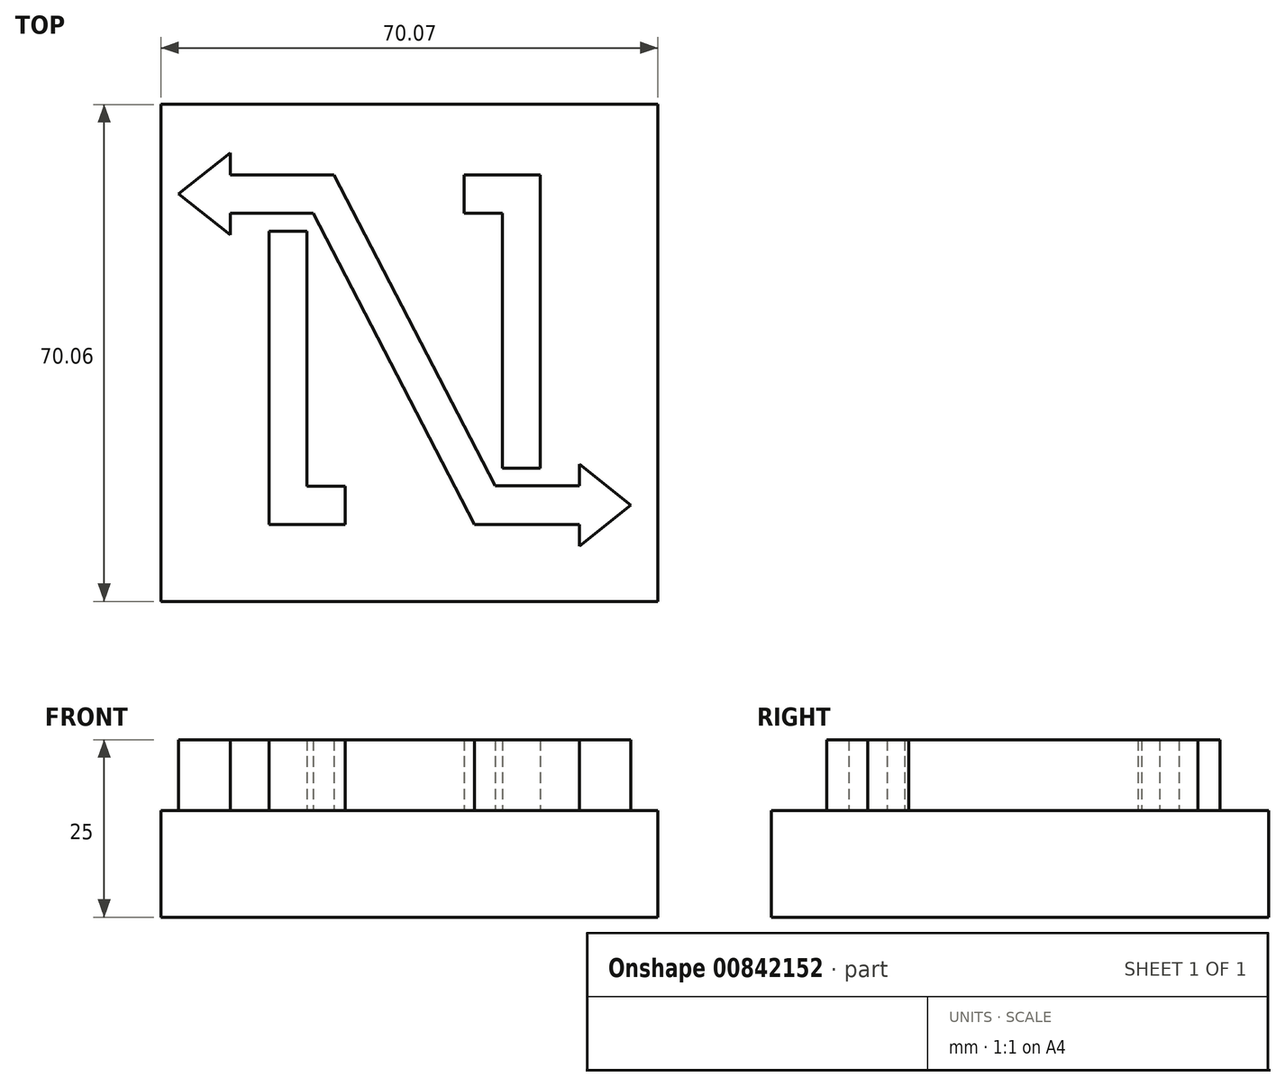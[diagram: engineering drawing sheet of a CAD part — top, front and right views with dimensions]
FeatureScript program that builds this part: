
annotation { "Feature Type Name" : "Feature", "Feature Type Description" : "" }
export const myFeature = defineFeature(function(context is Context, id is Id, definition is map)
    precondition{}
    {
        {
            var Q0;
            Q0=qCreatedBy(makeId("Top.planeOp"),FACE);
            var sketch = newSketch(context, id + "F0", { "sketchPlane" : qUnion([Q0])});
            skLineSegment(sketch, "E0.bottom", {"start": v(-34.77, 34.42) * mm, "end": v(35.3, 34.42) * mm});
            skLineSegment(sketch, "E0.top", {"start": v(-34.77, -35.64) * mm, "end": v(35.3, -35.64) * mm});
            skLineSegment(sketch, "E0.left", {"start": v(-34.77, 34.42) * mm, "end": v(-34.77, -35.64) * mm});
            skLineSegment(sketch, "E0.right", {"start": v(35.3, 34.42) * mm, "end": v(35.3, -35.64) * mm});
            skSolve(sketch);
        }
        {
            var Q0;
            Q0=qCreatedBy(makeId("Top.planeOp"),FACE);
            var sketch = newSketch(context, id + "F1", { "sketchPlane" : qUnion([Q0])});
            skLineSegment(sketch, "E1", {"start": v(-19.5, 16.57) * mm, "end": v(-19.5, -24.77) * mm});
            skLineSegment(sketch, "E2", {"start": v(-19.5, -24.77) * mm, "end": v(-14.17, -24.77) * mm});
            skLineSegment(sketch, "E3", {"start": v(-14.17, -24.77) * mm, "end": v(-14.17, 16.57) * mm});
            skLineSegment(sketch, "E4", {"start": v(-14.17, 16.57) * mm, "end": v(-19.5, 16.57) * mm});
            skLineSegment(sketch, "E5", {"start": v(-19.59, 24.5) * mm, "end": v(-25, 24.5) * mm});
            skLineSegment(sketch, "E6", {"start": v(-25, 19.09) * mm, "end": v(-19.59, 19.09) * mm});
            skLineSegment(sketch, "E7", {"start": v(-19.59, 19.09) * mm, "end": v(-13.31, 19.09) * mm});
            skLineSegment(sketch, "E8", {"start": v(-10.36, 24.5) * mm, "end": v(-19.59, 24.5) * mm});
            skLineSegment(sketch, "E9", {"start": v(-25, 24.5) * mm, "end": v(-25, 27.58) * mm});
            skLineSegment(sketch, "E10", {"start": v(-25, 27.58) * mm, "end": v(-32.28, 21.8) * mm});
            skLineSegment(sketch, "E11", {"start": v(-32.28, 21.8) * mm, "end": v(-25, 16) * mm});
            skLineSegment(sketch, "E12", {"start": v(-25, 19.09) * mm, "end": v(-25, 16) * mm});
            skLineSegment(sketch, "E13", {"start": v(-14.17, -24.77) * mm, "end": v(-8.77, -24.77) * mm});
            skLineSegment(sketch, "E14", {"start": v(-8.77, -24.77) * mm, "end": v(-8.77, -19.37) * mm});
            skLineSegment(sketch, "E15", {"start": v(-8.77, -19.37) * mm, "end": v(-14.17, -19.37) * mm});
            skLineSegment(sketch, "E16", {"start": v(-25, 24.5) * mm, "end": v(-25, 19.09) * mm, "construction": true});
            skLineSegment(sketch, "E17", {"start": v(18.7, -16.84) * mm, "end": v(18.7, 24.5) * mm});
            skLineSegment(sketch, "E18", {"start": v(18.7, 24.5) * mm, "end": v(13.38, 24.5) * mm});
            skLineSegment(sketch, "E19", {"start": v(13.38, 24.5) * mm, "end": v(13.38, -16.84) * mm});
            skLineSegment(sketch, "E20", {"start": v(13.38, -16.84) * mm, "end": v(18.7, -16.84) * mm});
            skLineSegment(sketch, "E21", {"start": v(18.8, -24.77) * mm, "end": v(24.2, -24.77) * mm});
            skLineSegment(sketch, "E22", {"start": v(24.2, -19.36) * mm, "end": v(18.8, -19.36) * mm});
            skLineSegment(sketch, "E23", {"start": v(18.8, -19.36) * mm, "end": v(12.36, -19.36) * mm});
            skLineSegment(sketch, "E24", {"start": v(9.4, -24.77) * mm, "end": v(18.8, -24.77) * mm});
            skLineSegment(sketch, "E25", {"start": v(24.2, -24.77) * mm, "end": v(24.2, -27.85) * mm});
            skLineSegment(sketch, "E26", {"start": v(24.2, -27.85) * mm, "end": v(31.48, -22.06) * mm});
            skLineSegment(sketch, "E27", {"start": v(31.48, -22.06) * mm, "end": v(24.2, -16.28) * mm});
            skLineSegment(sketch, "E28", {"start": v(24.2, -19.36) * mm, "end": v(24.2, -16.28) * mm});
            skLineSegment(sketch, "E29", {"start": v(13.38, 24.5) * mm, "end": v(7.98, 24.5) * mm});
            skLineSegment(sketch, "E30", {"start": v(7.98, 24.5) * mm, "end": v(7.98, 19.1) * mm});
            skLineSegment(sketch, "E31", {"start": v(7.98, 19.1) * mm, "end": v(13.38, 19.1) * mm});
            skLineSegment(sketch, "E32", {"start": v(24.2, -24.77) * mm, "end": v(24.2, -19.36) * mm, "construction": true});
            skLineSegment(sketch, "E33", {"start": v(-13.31, 19.09) * mm, "end": v(9.4, -24.77) * mm});
            skLineSegment(sketch, "E34", {"start": v(12.36, -19.36) * mm, "end": v(-10.36, 24.5) * mm});
            skSolve(sketch);
        }
        {
            var Q0;
            Q0 = qSketchRegion(id + "F0", true);
            extrude(context, id + "F2", {"entities" : qUnion([Q0]), "depth" : 15 * mm, "offsetDistance" : 25 * mm});
        }
        {
            var Q0;
            Q0 = qSketchRegion(id + "F1", true);
            extrude(context, id + "F3", {"entities" : qUnion([Q0]), "operationType" : NewBodyOperationType.ADD, "depth" : 25 * mm, "offsetDistance" : 25 * mm});
        }
    });
